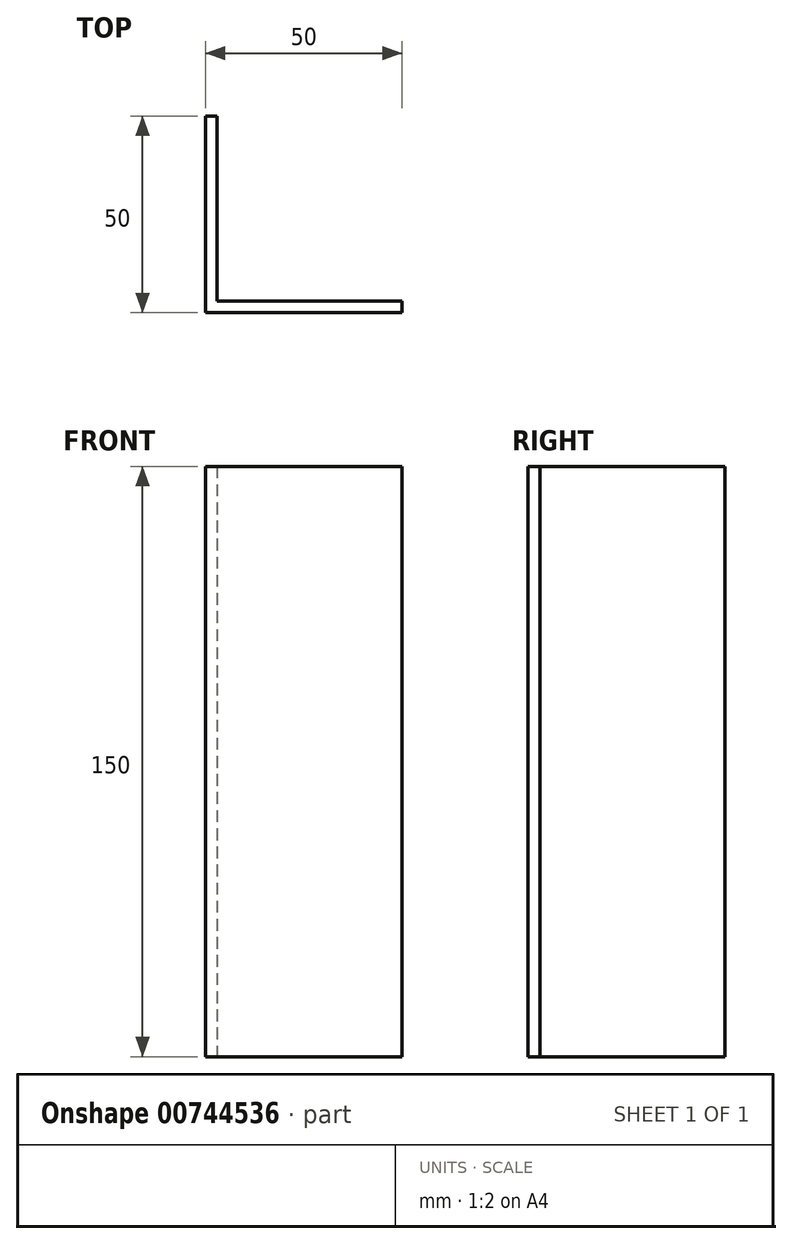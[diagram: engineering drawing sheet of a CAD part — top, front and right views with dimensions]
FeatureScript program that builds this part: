
annotation { "Feature Type Name" : "Feature", "Feature Type Description" : "" }
export const myFeature = defineFeature(function(context is Context, id is Id, definition is map)
    precondition{}
    {
        {
            var Q0;
            Q0=qCreatedBy(makeId("Top.planeOp"),FACE);
            var sketch = newSketch(context, id + "F0", { "sketchPlane" : qUnion([Q0])});
            skLineSegment(sketch, "E0", {"start": v(0, 0) * mm, "end": v(-50, 0) * mm});
            skLineSegment(sketch, "E1", {"start": v(-50, 0) * mm, "end": v(-50, 50) * mm});
            skLineSegment(sketch, "E2", {"start": v(-50, 50) * mm, "end": v(-47, 50) * mm});
            skLineSegment(sketch, "E3", {"start": v(0, 0) * mm, "end": v(0, 3) * mm});
            skLineSegment(sketch, "E4", {"start": v(0, 3) * mm, "end": v(-47, 3) * mm});
            skLineSegment(sketch, "E5", {"start": v(-47, 50) * mm, "end": v(-47, 3) * mm});
            skPoint(sketch, "E6.orphan", {"position": v(-47, 0) * mm});
            skSolve(sketch);
        }
        {
            var Q0;
            Q0 = qSketchRegion(id + "F0", true);
            extrude(context, id + "F1", {"entities" : qUnion([Q0]), "depth" : 150 * mm, "offsetDistance" : 25 * mm});
        }
    });
